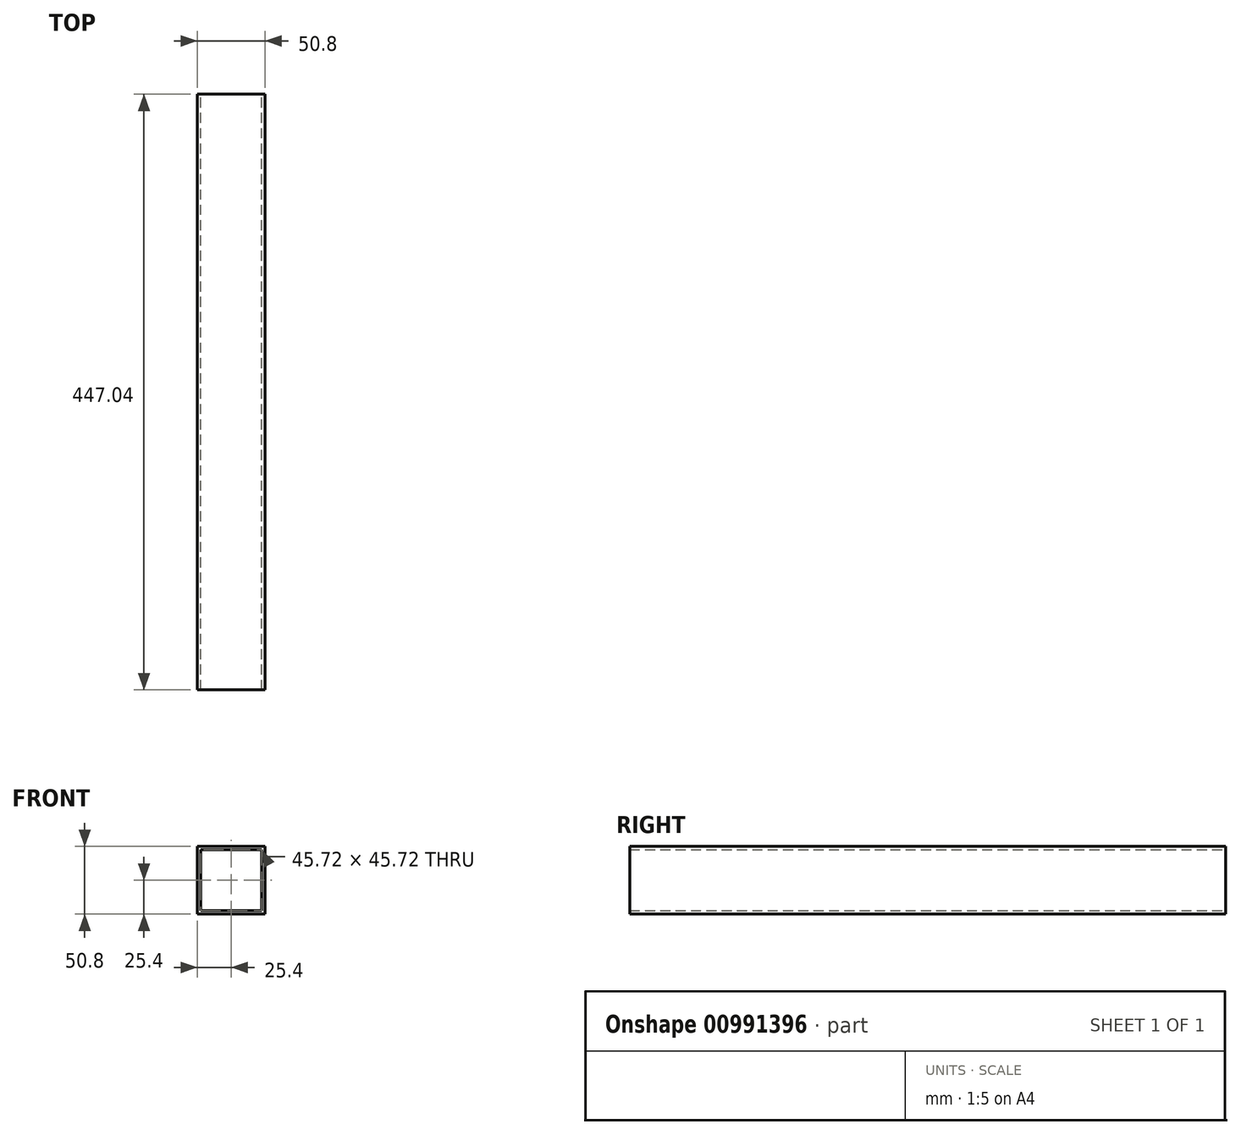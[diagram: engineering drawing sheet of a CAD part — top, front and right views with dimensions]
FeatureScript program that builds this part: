
annotation { "Feature Type Name" : "Feature", "Feature Type Description" : "" }
export const myFeature = defineFeature(function(context is Context, id is Id, definition is map)
    precondition{}
    {
        {
            var Q0;
            Q0=qCreatedBy(makeId("Front.planeOp"),FACE);
            var sketch = newSketch(context, id + "F0", { "sketchPlane" : qUnion([Q0])});
            skLineSegment(sketch, "E0.bottom", {"start": v(25.4, 25.4) * mm, "end": v(-25.4, 25.4) * mm});
            skLineSegment(sketch, "E0.top", {"start": v(25.4, -25.4) * mm, "end": v(-25.4, -25.4) * mm});
            skLineSegment(sketch, "E0.left", {"start": v(25.4, 25.4) * mm, "end": v(25.4, -25.4) * mm});
            skLineSegment(sketch, "E0.right", {"start": v(-25.4, 25.4) * mm, "end": v(-25.4, -25.4) * mm});
            skPoint(sketch, "E0.middle", {"position": v(0, 0) * mm});
            skLineSegment(sketch, "E1.0", {"start": v(-22.86, 22.86) * mm, "end": v(-22.86, -22.86) * mm});
            skLineSegment(sketch, "E1.1", {"start": v(22.86, 22.86) * mm, "end": v(-22.86, 22.86) * mm});
            skLineSegment(sketch, "E1.2", {"start": v(22.86, 22.86) * mm, "end": v(22.86, -22.86) * mm});
            skLineSegment(sketch, "E1.3", {"start": v(22.86, -22.86) * mm, "end": v(-22.86, -22.86) * mm});
            skSolve(sketch);
        }
        {
            var Q0;
            Q0=qSketchRegion(id+"F0",true);
            extrude(context, id + "F1", {"entities" : qUnion([Q0]), "endBound" : BoundingType.SYMMETRIC, "depth" : 447.04 * mm, "offsetDistance" : 25.4 * mm});
        }
    });
